# Revit family: Haworth_BuzziSpark_LoungeChair
name_source: partatom
category: Furniture
revit_build: Autodesk Revit 2018 (Build: 20170223_1515(x64)
units: mm (PartAtom-declared; Revit-internal decimal feet)

## family parameters
Always vertical = Yes
Cut with Voids When Loaded = No
OmniClass Number = 23.40.70.14.64.21
OmniClass Title = Systems Furniture
Room Calculation Point = No
Shared = No
Work Plane-Based = No

## types (2) — shared parameters
Actual Depth = 37.52 "
Actual Width = 51.69 "
Arm Offset = 5.52 "
Assembly Code = E2020200
Back Cushion Width = 35.55 "
Back Upholstery Width = 42.7 "
Manufacturer = Haworth
Middle Leg Control = No
Model = HCBZ-SKL1
Revision Number = 1
Seat Depth = 27.56 "
Seat Height = 17.72 "
Seat Width = 33.86 "
Side Upholstery Width = 25.5 "
Size = Verify Final Dim. w/ Haworth
URL - Product = https://www.haworth.com
Warranty = http://www.haworth.com
With Arm Cushion = Yes

## per-type parameters (varying)
| type | Actual Height | Description | High Back | Medium Back | URL |
| HCBZ-SKL1 - High Back | 65.08 " | Haworth BuzziSpark Lounge Chair High Back | Yes | No | https://www.haworth.com |
| HCBZ-SKL1 - Medium Back | 54.64 " | Haworth BuzziSpark Lounge Chair Medium Back | No | Yes | http://www.haworth.com |

## geometry (parser evidence)
native form markers: Sweep x15
no freeform markers — native parametric forms only
